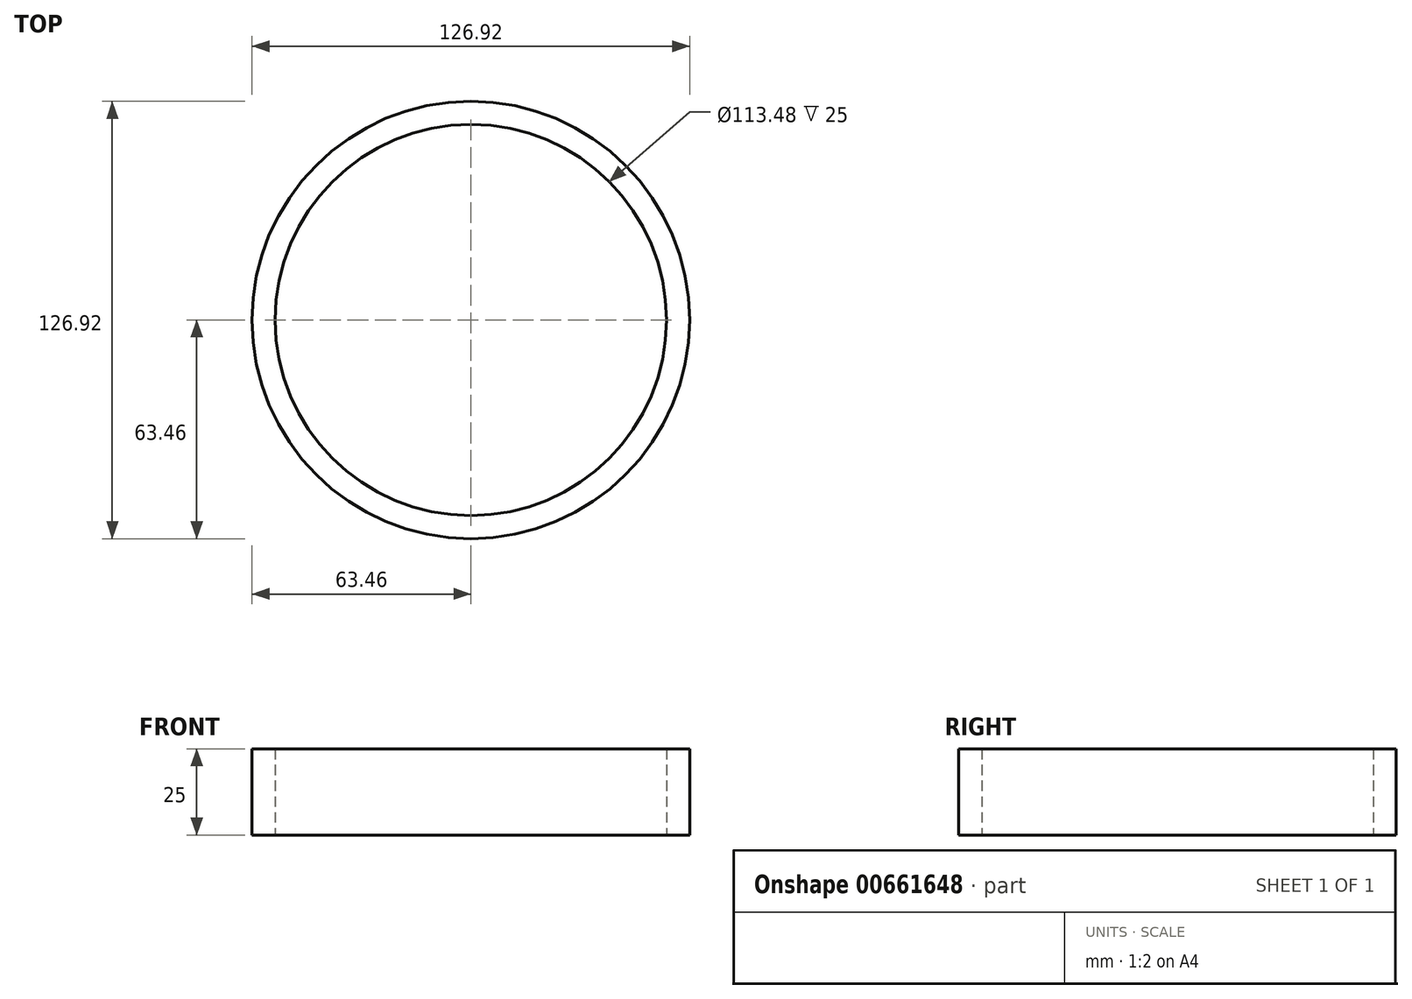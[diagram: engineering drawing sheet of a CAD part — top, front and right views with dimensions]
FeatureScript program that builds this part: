
annotation { "Feature Type Name" : "Feature", "Feature Type Description" : "" }
export const myFeature = defineFeature(function(context is Context, id is Id, definition is map)
    precondition{}
    {
        {
            var Q0;
            Q0=qCreatedBy(makeId("Top.planeOp"),FACE);
            var sketch = newSketch(context, id + "F0", { "sketchPlane" : qUnion([Q0])});
            skCircle(sketch, "E0", {"center": v(0, 0) * mm, "radius": 56.74 * mm});
            skCircle(sketch, "E1", {"center": v(0, 0) * mm, "radius": 63.46 * mm});
            skSolve(sketch);
        }
        {
            var Q0;
            Q0=makeQuery(id+"F0.imprint","IMPRINT",FACE,{"disambiguationData":[TD([[makeQuery(id+"F0.imprint","IMPRINT",EDGE,{"derivedFrom":sQuery(id+"F0.wireOp",EDGE,"E0")}),-1.0]])]});
            extrude(context, id + "F1", {"entities" : qUnion([Q0]), "depth" : 25 * mm, "offsetDistance" : 25 * mm});
        }
    });
